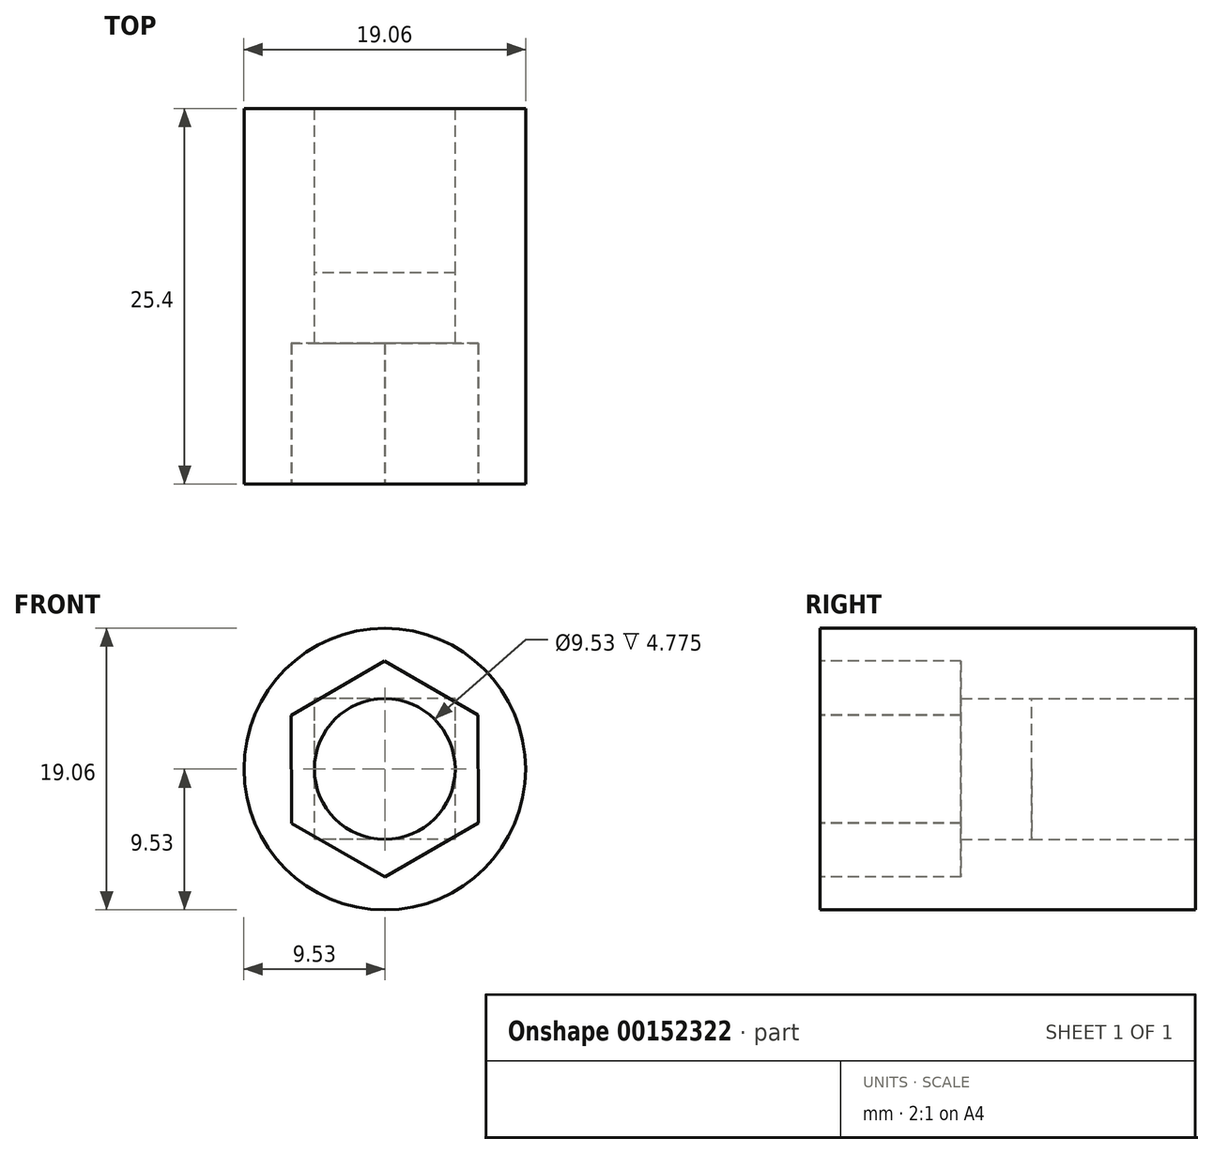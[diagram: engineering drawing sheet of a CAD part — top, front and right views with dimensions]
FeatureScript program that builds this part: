
annotation { "Feature Type Name" : "Feature", "Feature Type Description" : "" }
export const myFeature = defineFeature(function(context is Context, id is Id, definition is map)
    precondition{}
    {
        {
            var Q0;
            Q0=qCreatedBy(makeId("Front.planeOp"),FACE);
            var sketch = newSketch(context, id + "F0", { "sketchPlane" : qUnion([Q0])});
            skCircle(sketch, "E0", {"center": v(0, 0) * mm, "radius": 9.53 * mm});
            skSolve(sketch);
        }
        {
            var Q0;
            Q0 = qSketchRegion(id + "F0", true);
            extrude(context, id + "F1", {"entities" : qUnion([Q0]), "depth" : 25.4 * mm});
        }
        {
            var Q0;
            Q0=qCreatedBy(makeId("Front.planeOp"),FACE);
            var sketch = newSketch(context, id + "F2", { "sketchPlane" : qUnion([Q0])});
            skLineSegment(sketch, "E1.bottom", {"start": v(4.76, -4.76) * mm, "end": v(-4.76, -4.76) * mm});
            skLineSegment(sketch, "E1.top", {"start": v(4.76, 4.76) * mm, "end": v(-4.76, 4.76) * mm});
            skLineSegment(sketch, "E1.left", {"start": v(4.76, -4.76) * mm, "end": v(4.76, 4.76) * mm});
            skLineSegment(sketch, "E1.right", {"start": v(-4.76, -4.76) * mm, "end": v(-4.76, 4.76) * mm});
            skPoint(sketch, "E1.middle", {"position": v(0, 0) * mm});
            skCircle(sketch, "E2", {"center": v(0, 0) * mm, "radius": 4.76 * mm});
            skSolve(sketch);
        }
        {
            var Q0;
            Q0=makeQuery(id+"F1.opExtrude","CAP_FACE",FACE,{"disambiguationData":[OSD([sQuery(id+"F0.wireOp",EDGE,"E0")])],"isStart":true});
            var sketch = newSketch(context, id + "F3", { "sketchPlane" : qUnion([Q0])});
            skSolve(sketch);
        }
        {
            var Q0;
            Q0=makeQuery(id+"F3.imprint","IMPRINT",FACE,{"disambiguationData":[TD([[makeQuery(id+"F3.imprint","IMPRINT",EDGE,{"derivedFrom":makeQuery(id+"F1.opExtrude","CAP_EDGE",EDGE,{"disambiguationData":[OSD([sQuery(id+"F0.wireOp",EDGE,"E0")])],"isStart":true})}),-1.0]])]});
            var sketch = newSketch(context, id + "F4", { "sketchPlane" : qUnion([Q0])});
            skSolve(sketch);
        }
        {
            var Q0;
            Q0 = qSketchRegion(id + "F4", true);
            var Q1;
            {var subQ0=sQuery(id+"F2.wireOp",EDGE,"E2");var subQ1=makeQuery(id+"F2.imprint","INTERSECT",VERTEX,{"derivedFrom":[sQuery(id+"F2.wireOp",EDGE,"E1.top"),subQ0]});Q1=makeQuery(id+"F2.imprint","IMPRINT",FACE,{"disambiguationData":[TD([[makeQuery(id+"F2.imprint","IMPRINT",EDGE,{"disambiguationData":[TD([[subQ1,1.0]])],"derivedFrom":subQ0}),1.0]])]});}
            extrude(context, id + "F5", {"entities" : qUnion([Q0, Q1]), "operationType" : NewBodyOperationType.REMOVE, "endBound" : BoundingType.THROUGH_ALL, "depth" : 25.4 * mm});
        }
        {
            var Q0;
            Q0 = qSketchRegion(id + "F2", true);
            extrude(context, id + "F6", {"entities" : qUnion([Q0]), "operationType" : NewBodyOperationType.REMOVE, "depth" : 11.1 * mm});
        }
        {
            var Q0;
            Q0=makeQuery(id+"F1.opExtrude","CAP_FACE",FACE,{"disambiguationData":[OSD([sQuery(id+"F0.wireOp",EDGE,"E0")])],"isStart":false});
            var sketch = newSketch(context, id + "F7", { "sketchPlane" : qUnion([Q0])});
            skCircle(sketch, "E3.cCircle", {"center": v(0, 0) * mm, "radius": 6.32 * mm, "construction": true});
            skLineSegment(sketch, "E3.0", {"start": v(6.33, -3.64) * mm, "end": v(0.02, -7.3) * mm});
            skLineSegment(sketch, "E3.1", {"start": v(0.02, -7.3) * mm, "end": v(-6.32, -3.66) * mm});
            skLineSegment(sketch, "E3.2", {"start": v(-6.32, -3.66) * mm, "end": v(-6.33, 3.64) * mm});
            skLineSegment(sketch, "E3.3", {"start": v(-6.33, 3.64) * mm, "end": v(-0.02, 7.3) * mm});
            skLineSegment(sketch, "E3.4", {"start": v(-0.02, 7.3) * mm, "end": v(6.32, 3.66) * mm});
            skLineSegment(sketch, "E3.5", {"start": v(6.32, 3.66) * mm, "end": v(6.33, -3.64) * mm});
            skPoint(sketch, "E3.0.midPoint", {"position": v(3.17, -5.47) * mm});
            skSolve(sketch);
        }
        {
            var Q0;
            Q0 = qSketchRegion(id + "F7", true);
            extrude(context, id + "F8", {"entities" : qUnion([Q0]), "operationType" : NewBodyOperationType.REMOVE, "oppositeDirection" : true, "depth" : 9.52 * mm});
        }
    });
